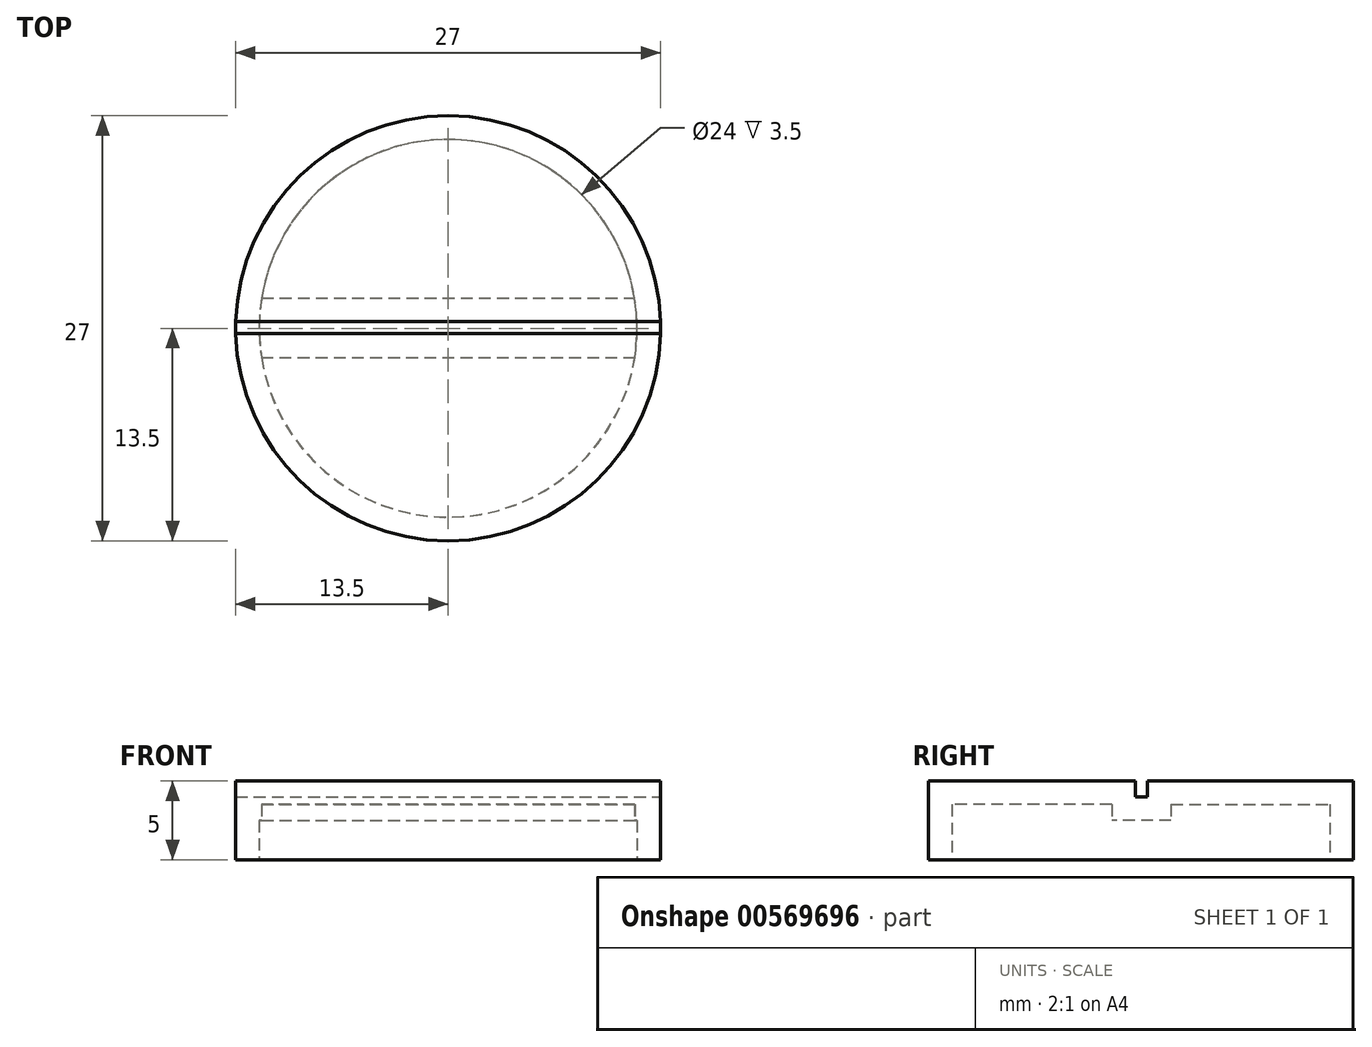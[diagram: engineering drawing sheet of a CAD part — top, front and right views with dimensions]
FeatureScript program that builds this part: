
annotation { "Feature Type Name" : "Feature", "Feature Type Description" : "" }
export const myFeature = defineFeature(function(context is Context, id is Id, definition is map)
    precondition{}
    {
        {
            var Q0;
            Q0=qCreatedBy(makeId("Top.planeOp"),FACE);
            var sketch = newSketch(context, id + "F0", { "sketchPlane" : qUnion([Q0])});
            skCircle(sketch, "E0", {"center": v(0, 0) * mm, "radius": 13.5 * mm});
            skLineSegment(sketch, "E1", {"start": v(-13.5, 0.43) * mm, "end": v(13.5, 0.43) * mm});
            skLineSegment(sketch, "E2", {"start": v(-13.5, -0.34) * mm, "end": v(13.5, -0.34) * mm});
            skSolve(sketch);
        }
        {
            var Q0;
            {var subQ0=sQuery(id+"F0.wireOp",EDGE,"E1");Q0=makeQuery(id+"F0.imprint","IMPRINT",FACE,{"disambiguationData":[TD([[makeQuery(id+"F0.imprint","IMPRINT",EDGE,{"derivedFrom":subQ0}),1.0]])]});}
            var Q1;
            {var subQ0=sQuery(id+"F0.wireOp",EDGE,"E2");Q1=makeQuery(id+"F0.imprint","IMPRINT",FACE,{"disambiguationData":[TD([[makeQuery(id+"F0.imprint","IMPRINT",EDGE,{"derivedFrom":subQ0}),-1.0]])]});}
            extrude(context, id + "F1", {"entities" : qUnion([Q0, Q1]), "depth" : 5 * mm, "offsetDistance" : 25 * mm});
        }
        {
            var Q0;
            {var subQ0=sQuery(id+"F0.wireOp",EDGE,"E1");Q0=makeQuery(id+"F0.imprint","IMPRINT",FACE,{"disambiguationData":[TD([[makeQuery(id+"F0.imprint","IMPRINT",EDGE,{"derivedFrom":subQ0}),-1.0]])]});}
            extrude(context, id + "F2", {"entities" : qUnion([Q0]), "depth" : 4 * mm, "offsetDistance" : 25 * mm});
        }
        {
            var Q0;
            Q0=makeQuery(id+"F1.opExtrude","SWEPT_BODY",BODY,{"disambiguationData":[OSD([sQuery(id+"F0.wireOp",EDGE,"E0"),sQuery(id+"F0.wireOp",EDGE,"E1")])]});
            var Q1;
            Q1=makeQuery(id+"F1.opExtrude","SWEPT_BODY",BODY,{"disambiguationData":[OSD([sQuery(id+"F0.wireOp",EDGE,"E0"),sQuery(id+"F0.wireOp",EDGE,"E2")])]});
            var Q2;
            Q2=makeQuery(id+"F2.opExtrude","SWEPT_BODY",BODY,{"disambiguationData":[OSD([sQuery(id+"F0.wireOp",EDGE,"E0"),sQuery(id+"F0.wireOp",EDGE,"E1"),sQuery(id+"F0.wireOp",EDGE,"E2")])]});
            booleanBodies(context, id + "F3", {"operationType" : BooleanOperationType.UNION, "tools" : qUnion([Q0, Q1, Q2])});
        }
        {
            var Q0;
            {var subQ0=sQuery(id+"F0.wireOp",EDGE,"E2");var subQ1=sQuery(id+"F0.wireOp",EDGE,"E1");var subQ2=sQuery(id+"F0.wireOp",EDGE,"E0");Q0=makeQuery(id+"F3.opBoolean","MERGE",FACE,{"derivedFrom":[makeQuery(id+"F1.opExtrude","CAP_FACE",FACE,{"disambiguationData":[OSD([subQ2,subQ1])],"isStart":true}),makeQuery(id+"F1.opExtrude","CAP_FACE",FACE,{"disambiguationData":[OSD([subQ2,subQ0])],"isStart":true}),makeQuery(id+"F2.opExtrude","CAP_FACE",FACE,{"disambiguationData":[OSD([subQ2,subQ1,subQ0])],"isStart":true})]});}
            shell(context, id + "F4", {"entities" : qUnion([Q0]), "thickness" : 1.5 * mm});
        }
    });
